# Revit family: Toilet-Wall_Mount-KOHLER-PATIO-K-4187IN.rfa_
name_source: partatom
category: Plumbing Fixtures
units: mm (PartAtom-declared; Revit-internal decimal feet)

## family parameters
Cut with Voids When Loaded = No
Host = Face
OmniClass Number = 23.31.19.00
OmniClass Title = Toilets
Part Type = Normal
Room Calculation Point = No
Round Connector Dimension = Use Diameter
Shared = No

## types (5) — shared parameters
ADA Compliant = No
Assembly Code = D2010100
CW Connection = Yes
Cold Water Inlet = Cold Water Inlet
Date Modified = 06/21/2024
Default Elevation = 0"
Description = WALL HUNG BOWL WITH FLUSH DIVERTER
Flow Rate = 0 GPM
Flush Rate- GPF = GPF
Flush Rate- LPF = LPF
HW Connection = No
Hot Water Inlet = Hot Water Inlet
Length = 21 3/8"
Manufacturer = Kohler Co.
Master Format 2014 = 22 42 13.13
Master Format 2014 Name = Residential Water Closets
Material = Viterious China
Pressure = 0.00 psi
Product Name = PATIO
Seat Included = No
URL = https://www.kohler.co.in
Vent Connection = No
Waste Connection = Yes
Waste Water Outlet = Waste Water Outlet
WaterSense Certified = No
Width = 14 13/16"

## per-type parameters (varying)
| type | Finish | Model | Seat Finish | Type |
| 0-White | Kohler-Vitreous_China-0-White | K-4187IN-WD-0 | Kohler-Plastic-0-White | 1 |
| 47-Almond | Kohler-Vitreous_China-47-Almond | K-4187IN-WD-47 | Kohler-Plastic-47-Almond | 2 |
| 7-Black Black | Kohler-Vitreous_China-7-Black_Black | K-4187IN-WD-7 | Kohler-Plastic-7-Black_Black | 3 |
| 96-Biscuit | Kohler-Vitreous_China-96-Biscuit | K-4187IN-WD-96 | Kohler-Plastic-96-Biscuit | 4 |
| 58-Thunder Grey | Kohler-Vitreous_China-58-Thunder_Grey | K-4187IN-WD-58 | Kohler-Plastic-58-Thunder_Grey | 5 |

## geometry (parser evidence)
native form markers: Sweep x8
no freeform markers — native parametric forms only
